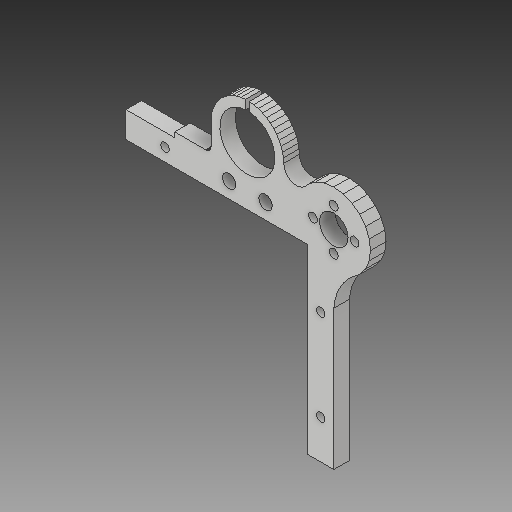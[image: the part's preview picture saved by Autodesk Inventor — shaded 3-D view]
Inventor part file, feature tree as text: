
AUTODESK INVENTOR PART (.ipt)
format: ipt  version: 2017 (Build 210142000, 142)  size: 295,936 bytes
history: native  units: mm
features: sketch x4, other x3
ambient origin geometry x8: Origin, YZ Plane, XZ Plane, XY Plane, X Axis, Y Axis, Z Axis, Center Point
bodies: Solid1 (feature_tree)
feature tree (7):
  other  "Left Bed Holder Mid.ipt"
  other  "Solid1::Left Bed Holder Mid.ipt"
  other  "TaggingFeature1"
  sketch  "Sketch1"  dims[d0=10.0mm]
  sketch  "Sketch2"
  sketch  "Sketch3"
  sketch  "Sketch4"
